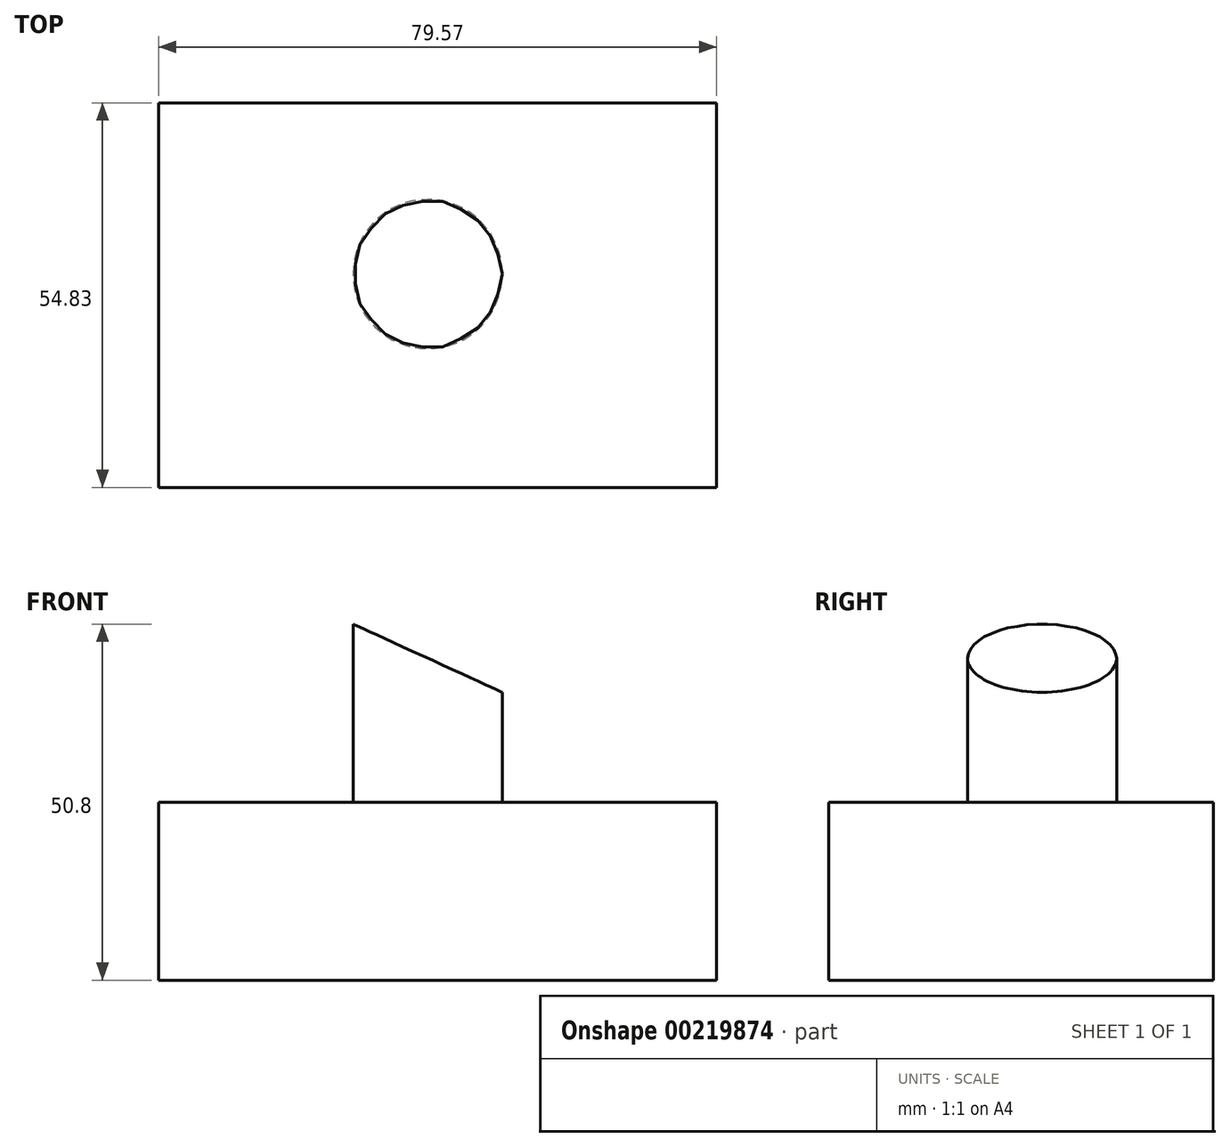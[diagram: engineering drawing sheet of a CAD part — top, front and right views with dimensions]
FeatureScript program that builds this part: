
annotation { "Feature Type Name" : "Feature", "Feature Type Description" : "" }
export const myFeature = defineFeature(function(context is Context, id is Id, definition is map)
    precondition{}
    {
        {
            var Q0;
            Q0=qCreatedBy(makeId("Top.planeOp"),FACE);
            var sketch = newSketch(context, id + "F0", { "sketchPlane" : qUnion([Q0])});
            skLineSegment(sketch, "E0.bottom", {"start": v(-50.86, 33) * mm, "end": v(28.71, 33) * mm});
            skLineSegment(sketch, "E0.top", {"start": v(-50.86, -21.83) * mm, "end": v(28.71, -21.83) * mm});
            skLineSegment(sketch, "E0.left", {"start": v(-50.86, 33) * mm, "end": v(-50.86, -21.83) * mm});
            skLineSegment(sketch, "E0.right", {"start": v(28.71, 33) * mm, "end": v(28.71, -21.83) * mm});
            skSolve(sketch);
        }
        {
            var Q0;
            Q0 = qSketchRegion(id + "F0", true);
            extrude(context, id + "F1", {"entities" : qUnion([Q0]), "depth" : 25.4 * mm});
        }
        {
            var Q0;
            Q0=makeQuery(id+"F1.opExtrude","CAP_FACE",FACE,{"disambiguationData":[OSD([sQuery(id+"F0.wireOp",EDGE,"E0.bottom"),sQuery(id+"F0.wireOp",EDGE,"E0.top"),sQuery(id+"F0.wireOp",EDGE,"E0.left"),sQuery(id+"F0.wireOp",EDGE,"E0.right")])],"isStart":false});
            var sketch = newSketch(context, id + "F2", { "sketchPlane" : qUnion([Q0])});
            skCircle(sketch, "E1", {"center": v(-12.5, 8.6) * mm, "radius": 10.63 * mm});
            skSolve(sketch);
        }
        {
            var Q0;
            Q0=makeQuery(id+"F2.imprint","IMPRINT",FACE,{"disambiguationData":[TD([[makeQuery(id+"F2.imprint","IMPRINT",EDGE,{"derivedFrom":sQuery(id+"F2.wireOp",EDGE,"E1")}),1.0]])]});
            extrude(context, id + "F3", {"entities" : qUnion([Q0]), "operationType" : NewBodyOperationType.ADD, "depth" : 25.4 * mm});
        }
        {
            var Q0;
            Q0=qCreatedBy(makeId("Front.planeOp"),FACE);
            var sketch = newSketch(context, id + "F4", { "sketchPlane" : qUnion([Q0])});
            skLineSegment(sketch, "E2", {"start": v(-23.26, 50.86) * mm, "end": v(-1.41, 50.86) * mm});
            skLineSegment(sketch, "E3", {"start": v(-1.41, 50.86) * mm, "end": v(-1.41, 40.86) * mm});
            skLineSegment(sketch, "E4", {"start": v(-1.41, 40.86) * mm, "end": v(-23.26, 50.86) * mm});
            skSolve(sketch);
        }
        {
            var Q0;
            Q0 = qSketchRegion(id + "F4", true);
            extrude(context, id + "F5", {"entities" : qUnion([Q0]), "operationType" : NewBodyOperationType.REMOVE, "oppositeDirection" : true, "depth" : 27.18 * mm, "hasSecondDirection" : true, "secondDirectionOppositeDirection" : false, "secondDirectionDepth" : 32.77 * mm});
        }
    });
